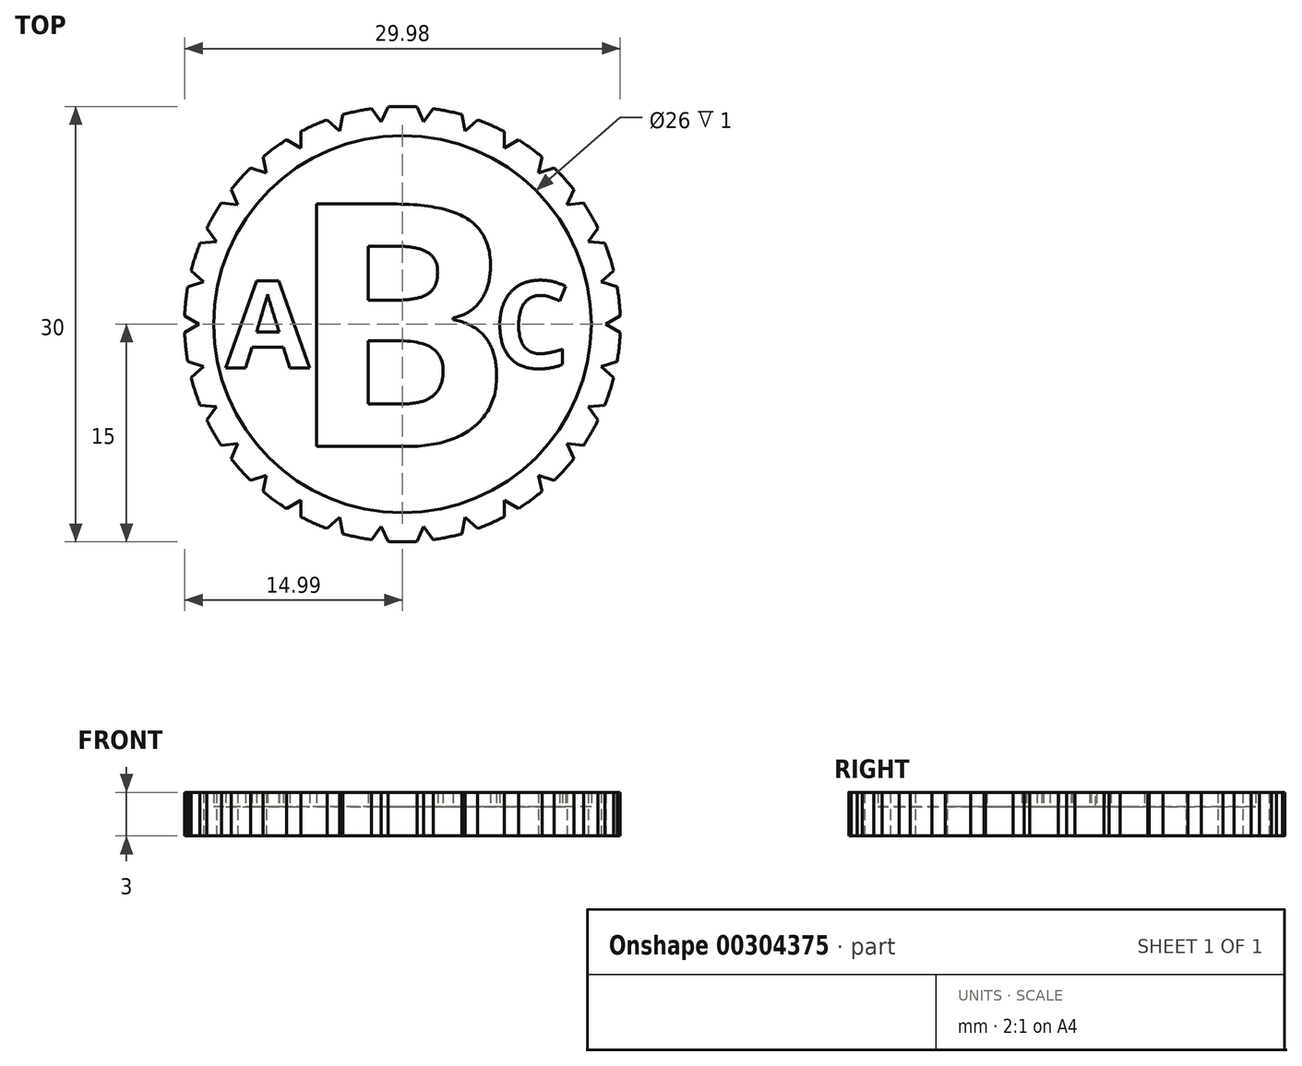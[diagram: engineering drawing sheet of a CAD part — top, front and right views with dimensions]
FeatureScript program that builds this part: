
annotation { "Feature Type Name" : "Feature", "Feature Type Description" : "" }
export const myFeature = defineFeature(function(context is Context, id is Id, definition is map)
    precondition{}
    {
        {
            var Q0;
            Q0=qCreatedBy(makeId("Top.planeOp"),FACE);
            var sketch = newSketch(context, id + "F0", { "sketchPlane" : qUnion([Q0])});
            skCircle(sketch, "E0", {"center": v(0, 0) * mm, "radius": 15 * mm});
            skCircle(sketch, "E1", {"center": v(0, 0) * mm, "radius": 13 * mm});
            skSolve(sketch);
        }
        {
            var Q0;
            Q0=makeQuery(id+"F0.imprint","IMPRINT",FACE,{"disambiguationData":[TD([[makeQuery(id+"F0.imprint","IMPRINT",EDGE,{"derivedFrom":sQuery(id+"F0.wireOp",EDGE,"98c0a119-c8f4-4081-9516-8cf6b4f2074b.sketch_text.stroke-0")}),-1.0]])]});
            var Q1;
            Q1=makeQuery(id+"F0.imprint","IMPRINT",FACE,{"disambiguationData":[TD([[makeQuery(id+"F0.imprint","IMPRINT",EDGE,{"derivedFrom":sQuery(id+"F0.wireOp",EDGE,"E0")}),1.0]])]});
            var Q2;
            Q2=makeQuery(id+"F0.imprint","IMPRINT",FACE,{"disambiguationData":[TD([[makeQuery(id+"F0.imprint","IMPRINT",EDGE,{"derivedFrom":sQuery(id+"F0.wireOp",EDGE,"3K3uGTc4-7jGt-BvkY-ZocM-s7WTgBB0BZUb")}),1.0]])]});
            var Q3;
            Q3=makeQuery(id+"F0.imprint","IMPRINT",FACE,{"disambiguationData":[TD([[makeQuery(id+"F0.imprint","IMPRINT",EDGE,{"derivedFrom":sQuery(id+"F0.wireOp",EDGE,"8gNE9ajH-bN55-gDtx-BwzA-LkQ6nyKFbA6s")}),1.0]])]});
            extrude(context, id + "F1", {"entities" : qUnion([Q0, Q1, Q2, Q3]), "depth" : 3 * mm});
        }
        {
            var Q0;
            Q0=makeQuery(id+"F0.imprint","IMPRINT",FACE,{"disambiguationData":[TD([[makeQuery(id+"F0.imprint","IMPRINT",EDGE,{"derivedFrom":sQuery(id+"F0.wireOp",EDGE,"E1")}),1.0]])]});
            var Q1;
            Q1=makeQuery(id+"F0.imprint","IMPRINT",FACE,{"disambiguationData":[TD([[makeQuery(id+"F0.imprint","IMPRINT",EDGE,{"derivedFrom":sQuery(id+"F0.wireOp",EDGE,"98c0a119-c8f4-4081-9516-8cf6b4f2074b.sketch_text.stroke-19")}),1.0]])]});
            var Q2;
            Q2=makeQuery(id+"F0.imprint","IMPRINT",FACE,{"disambiguationData":[TD([[makeQuery(id+"F0.imprint","IMPRINT",EDGE,{"derivedFrom":sQuery(id+"F0.wireOp",EDGE,"98c0a119-c8f4-4081-9516-8cf6b4f2074b.sketch_text.stroke-12")}),1.0]])]});
            extrude(context, id + "F2", {"entities" : qUnion([Q0, Q1, Q2]), "operationType" : NewBodyOperationType.ADD, "depth" : 2 * mm});
        }
        {
            var Q0;
            Q0=qCreatedBy(makeId("Top.planeOp"),FACE);
            var sketch = newSketch(context, id + "F3", { "sketchPlane" : qUnion([Q0])});
            skText(sketch, "E2", { "text": "B", "fontName": "OpenSans-Bold.ttf"});
            skText(sketch, "E3", { "text": "A", "fontName": "OpenSans-Bold.ttf"});
            skText(sketch, "E4", { "text": "C", "fontName": "OpenSans-Bold.ttf"});
            skLineSegment(sketch, "E5", {"start": v(-9, 0) * mm, "end": v(9, 0) * mm, "construction": true});
            const initialGuessF3  = {"E2": [-0.008, -0.00842, 1, 0, 0.01684], "E3": [-0.01215, -0.003, 1, 0, 0.006], "E4": [0.00622, -0.003, 1, 0, 0.006]};
            skSetInitialGuess(sketch, initialGuessF3);
            skSolve(sketch);
        }
        {
            var Q0;
            Q0 = qSketchRegion(id + "F3", true);
            extrude(context, id + "F4", {"entities" : qUnion([Q0]), "operationType" : NewBodyOperationType.ADD, "depth" : 3 * mm});
        }
        {
            var Q0;
            Q0=qCreatedBy(makeId("Top.planeOp"),FACE);
            var sketch = newSketch(context, id + "F5", { "sketchPlane" : qUnion([Q0])});
            skLineSegment(sketch, "E6", {"start": v(-18.33, 2.5) * mm, "end": v(-14, 0) * mm});
            skLineSegment(sketch, "E7", {"start": v(-14, 0) * mm, "end": v(-18.33, -2.5) * mm});
            skLineSegment(sketch, "E8", {"start": v(-18.33, -2.5) * mm, "end": v(-18.33, 2.5) * mm});
            skLineSegment(sketch, "E9.1.0", {"start": v(-18.45, -1.37) * mm, "end": v(-13.7, -2.91) * mm});
            skLineSegment(sketch, "E9.1.1", {"start": v(-13.7, -2.91) * mm, "end": v(-17.4, -6.26) * mm});
            skLineSegment(sketch, "E9.1.2", {"start": v(-17.4, -6.26) * mm, "end": v(-18.45, -1.37) * mm});
            skLineSegment(sketch, "E9.2.0", {"start": v(-17.76, -5.17) * mm, "end": v(-12.79, -5.7) * mm});
            skLineSegment(sketch, "E9.2.1", {"start": v(-12.79, -5.7) * mm, "end": v(-15.73, -9.74) * mm});
            skLineSegment(sketch, "E9.2.2", {"start": v(-15.73, -9.74) * mm, "end": v(-17.76, -5.17) * mm});
            skLineSegment(sketch, "E9.3.0", {"start": v(-16.3, -8.75) * mm, "end": v(-11.33, -8.23) * mm});
            skLineSegment(sketch, "E9.3.1", {"start": v(-11.33, -8.23) * mm, "end": v(-13.36, -12.8) * mm});
            skLineSegment(sketch, "E9.3.2", {"start": v(-13.36, -12.8) * mm, "end": v(-16.3, -8.75) * mm});
            skLineSegment(sketch, "E9.4.0", {"start": v(-14.12, -11.95) * mm, "end": v(-9.37, -10.4) * mm});
            skLineSegment(sketch, "E9.4.1", {"start": v(-9.37, -10.4) * mm, "end": v(-10.4, -15.3) * mm});
            skLineSegment(sketch, "E9.4.2", {"start": v(-10.4, -15.3) * mm, "end": v(-14.12, -11.95) * mm});
            skLineSegment(sketch, "E9.5.0", {"start": v(-11.33, -14.62) * mm, "end": v(-7, -12.12) * mm});
            skLineSegment(sketch, "E9.5.1", {"start": v(-7, -12.12) * mm, "end": v(-7, -17.12) * mm});
            skLineSegment(sketch, "E9.5.2", {"start": v(-7, -17.12) * mm, "end": v(-11.33, -14.62) * mm});
            skLineSegment(sketch, "E9.6.0", {"start": v(-8.04, -16.66) * mm, "end": v(-4.33, -13.31) * mm});
            skLineSegment(sketch, "E9.6.1", {"start": v(-4.33, -13.31) * mm, "end": v(-3.29, -18.2) * mm});
            skLineSegment(sketch, "E9.6.2", {"start": v(-3.29, -18.2) * mm, "end": v(-8.04, -16.66) * mm});
            skLineSegment(sketch, "E9.7.0", {"start": v(-4.4, -17.97) * mm, "end": v(-1.46, -13.92) * mm});
            skLineSegment(sketch, "E9.7.1", {"start": v(-1.46, -13.92) * mm, "end": v(0.57, -18.5) * mm});
            skLineSegment(sketch, "E9.7.2", {"start": v(0.57, -18.5) * mm, "end": v(-4.4, -17.97) * mm});
            skLineSegment(sketch, "E9.8.0", {"start": v(-0.57, -18.5) * mm, "end": v(1.46, -13.92) * mm});
            skLineSegment(sketch, "E9.8.1", {"start": v(1.46, -13.92) * mm, "end": v(4.4, -17.97) * mm});
            skLineSegment(sketch, "E9.8.2", {"start": v(4.4, -17.97) * mm, "end": v(-0.57, -18.5) * mm});
            skLineSegment(sketch, "E9.9.0", {"start": v(3.29, -18.2) * mm, "end": v(4.33, -13.31) * mm});
            skLineSegment(sketch, "E9.9.1", {"start": v(4.33, -13.31) * mm, "end": v(8.04, -16.66) * mm});
            skLineSegment(sketch, "E9.9.2", {"start": v(8.04, -16.66) * mm, "end": v(3.29, -18.2) * mm});
            skLineSegment(sketch, "E9.10.0", {"start": v(7, -17.12) * mm, "end": v(7, -12.12) * mm});
            skLineSegment(sketch, "E9.10.1", {"start": v(7, -12.12) * mm, "end": v(11.33, -14.62) * mm});
            skLineSegment(sketch, "E9.10.2", {"start": v(11.33, -14.62) * mm, "end": v(7, -17.12) * mm});
            skLineSegment(sketch, "E9.11.0", {"start": v(10.4, -15.3) * mm, "end": v(9.37, -10.4) * mm});
            skLineSegment(sketch, "E9.11.1", {"start": v(9.37, -10.4) * mm, "end": v(14.12, -11.95) * mm});
            skLineSegment(sketch, "E9.11.2", {"start": v(14.12, -11.95) * mm, "end": v(10.4, -15.3) * mm});
            skLineSegment(sketch, "E9.12.0", {"start": v(13.36, -12.8) * mm, "end": v(11.33, -8.23) * mm});
            skLineSegment(sketch, "E9.12.1", {"start": v(11.33, -8.23) * mm, "end": v(16.3, -8.75) * mm});
            skLineSegment(sketch, "E9.12.2", {"start": v(16.3, -8.75) * mm, "end": v(13.36, -12.8) * mm});
            skLineSegment(sketch, "E9.13.0", {"start": v(15.73, -9.74) * mm, "end": v(12.79, -5.7) * mm});
            skLineSegment(sketch, "E9.13.1", {"start": v(12.79, -5.7) * mm, "end": v(17.76, -5.17) * mm});
            skLineSegment(sketch, "E9.13.2", {"start": v(17.76, -5.17) * mm, "end": v(15.73, -9.74) * mm});
            skLineSegment(sketch, "E9.14.0", {"start": v(17.4, -6.26) * mm, "end": v(13.7, -2.91) * mm});
            skLineSegment(sketch, "E9.14.1", {"start": v(13.7, -2.91) * mm, "end": v(18.45, -1.37) * mm});
            skLineSegment(sketch, "E9.14.2", {"start": v(18.45, -1.37) * mm, "end": v(17.4, -6.26) * mm});
            skLineSegment(sketch, "E9.15.0", {"start": v(18.33, -2.5) * mm, "end": v(14, 0) * mm});
            skLineSegment(sketch, "E9.15.1", {"start": v(14, 0) * mm, "end": v(18.33, 2.5) * mm});
            skLineSegment(sketch, "E9.15.2", {"start": v(18.33, 2.5) * mm, "end": v(18.33, -2.5) * mm});
            skLineSegment(sketch, "E9.16.0", {"start": v(18.45, 1.37) * mm, "end": v(13.7, 2.91) * mm});
            skLineSegment(sketch, "E9.16.1", {"start": v(13.7, 2.91) * mm, "end": v(17.4, 6.26) * mm});
            skLineSegment(sketch, "E9.16.2", {"start": v(17.4, 6.26) * mm, "end": v(18.45, 1.37) * mm});
            skLineSegment(sketch, "E9.17.0", {"start": v(17.76, 5.17) * mm, "end": v(12.79, 5.7) * mm});
            skLineSegment(sketch, "E9.17.1", {"start": v(12.79, 5.7) * mm, "end": v(15.73, 9.74) * mm});
            skLineSegment(sketch, "E9.17.2", {"start": v(15.73, 9.74) * mm, "end": v(17.76, 5.17) * mm});
            skLineSegment(sketch, "E9.18.0", {"start": v(16.3, 8.75) * mm, "end": v(11.33, 8.23) * mm});
            skLineSegment(sketch, "E9.18.1", {"start": v(11.33, 8.23) * mm, "end": v(13.36, 12.8) * mm});
            skLineSegment(sketch, "E9.18.2", {"start": v(13.36, 12.8) * mm, "end": v(16.3, 8.75) * mm});
            skLineSegment(sketch, "E9.19.0", {"start": v(14.12, 11.95) * mm, "end": v(9.37, 10.4) * mm});
            skLineSegment(sketch, "E9.19.1", {"start": v(9.37, 10.4) * mm, "end": v(10.4, 15.3) * mm});
            skLineSegment(sketch, "E9.19.2", {"start": v(10.4, 15.3) * mm, "end": v(14.12, 11.95) * mm});
            skLineSegment(sketch, "E9.20.0", {"start": v(11.33, 14.62) * mm, "end": v(7, 12.12) * mm});
            skLineSegment(sketch, "E9.20.1", {"start": v(7, 12.12) * mm, "end": v(7, 17.12) * mm});
            skLineSegment(sketch, "E9.20.2", {"start": v(7, 17.12) * mm, "end": v(11.33, 14.62) * mm});
            skLineSegment(sketch, "E9.21.0", {"start": v(8.04, 16.66) * mm, "end": v(4.33, 13.31) * mm});
            skLineSegment(sketch, "E9.21.1", {"start": v(4.33, 13.31) * mm, "end": v(3.29, 18.2) * mm});
            skLineSegment(sketch, "E9.21.2", {"start": v(3.29, 18.2) * mm, "end": v(8.04, 16.66) * mm});
            skLineSegment(sketch, "E9.22.0", {"start": v(4.4, 17.97) * mm, "end": v(1.46, 13.92) * mm});
            skLineSegment(sketch, "E9.22.1", {"start": v(1.46, 13.92) * mm, "end": v(-0.57, 18.5) * mm});
            skLineSegment(sketch, "E9.22.2", {"start": v(-0.57, 18.5) * mm, "end": v(4.4, 17.97) * mm});
            skLineSegment(sketch, "E9.23.0", {"start": v(0.57, 18.5) * mm, "end": v(-1.46, 13.92) * mm});
            skLineSegment(sketch, "E9.23.1", {"start": v(-1.46, 13.92) * mm, "end": v(-4.4, 17.97) * mm});
            skLineSegment(sketch, "E9.23.2", {"start": v(-4.4, 17.97) * mm, "end": v(0.57, 18.5) * mm});
            skLineSegment(sketch, "E9.24.0", {"start": v(-3.29, 18.2) * mm, "end": v(-4.33, 13.31) * mm});
            skLineSegment(sketch, "E9.24.1", {"start": v(-4.33, 13.31) * mm, "end": v(-8.04, 16.66) * mm});
            skLineSegment(sketch, "E9.24.2", {"start": v(-8.04, 16.66) * mm, "end": v(-3.29, 18.2) * mm});
            skLineSegment(sketch, "E9.25.0", {"start": v(-7, 17.12) * mm, "end": v(-7, 12.12) * mm});
            skLineSegment(sketch, "E9.25.1", {"start": v(-7, 12.12) * mm, "end": v(-11.33, 14.62) * mm});
            skLineSegment(sketch, "E9.25.2", {"start": v(-11.33, 14.62) * mm, "end": v(-7, 17.12) * mm});
            skLineSegment(sketch, "E9.26.0", {"start": v(-10.4, 15.3) * mm, "end": v(-9.37, 10.4) * mm});
            skLineSegment(sketch, "E9.26.1", {"start": v(-9.37, 10.4) * mm, "end": v(-14.12, 11.95) * mm});
            skLineSegment(sketch, "E9.26.2", {"start": v(-14.12, 11.95) * mm, "end": v(-10.4, 15.3) * mm});
            skLineSegment(sketch, "E9.27.0", {"start": v(-13.36, 12.8) * mm, "end": v(-11.33, 8.23) * mm});
            skLineSegment(sketch, "E9.27.1", {"start": v(-11.33, 8.23) * mm, "end": v(-16.3, 8.75) * mm});
            skLineSegment(sketch, "E9.27.2", {"start": v(-16.3, 8.75) * mm, "end": v(-13.36, 12.8) * mm});
            skLineSegment(sketch, "E9.28.0", {"start": v(-15.73, 9.74) * mm, "end": v(-12.79, 5.7) * mm});
            skLineSegment(sketch, "E9.28.1", {"start": v(-12.79, 5.7) * mm, "end": v(-17.76, 5.17) * mm});
            skLineSegment(sketch, "E9.28.2", {"start": v(-17.76, 5.17) * mm, "end": v(-15.73, 9.74) * mm});
            skLineSegment(sketch, "E9.29.0", {"start": v(-17.4, 6.26) * mm, "end": v(-13.7, 2.91) * mm});
            skLineSegment(sketch, "E9.29.1", {"start": v(-13.7, 2.91) * mm, "end": v(-18.45, 1.37) * mm});
            skLineSegment(sketch, "E9.29.2", {"start": v(-18.45, 1.37) * mm, "end": v(-17.4, 6.26) * mm});
            skPoint(sketch, "E9.center", {"position": v(0, 0) * mm});
            skSolve(sketch);
        }
        {
            var Q0;
            Q0 = qSketchRegion(id + "F5", true);
            extrude(context, id + "F6", {"entities" : qUnion([Q0]), "operationType" : NewBodyOperationType.REMOVE, "depth" : 25 * mm});
        }
    });
